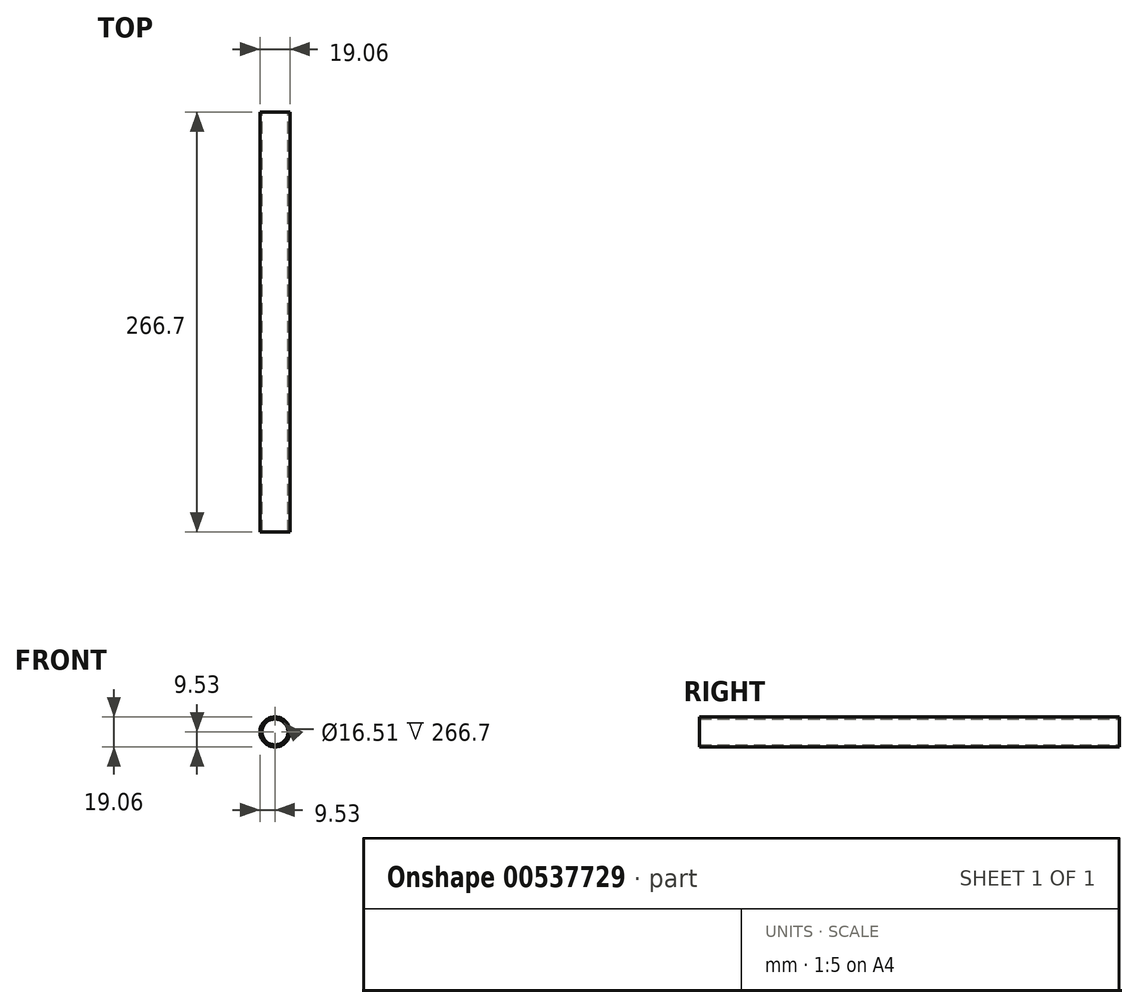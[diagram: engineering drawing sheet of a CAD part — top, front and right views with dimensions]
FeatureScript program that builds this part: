
annotation { "Feature Type Name" : "Feature", "Feature Type Description" : "" }
export const myFeature = defineFeature(function(context is Context, id is Id, definition is map)
    precondition{}
    {
        {
            var Q0;
            Q0=qCreatedBy(makeId("Front.planeOp"),FACE);
            var sketch = newSketch(context, id + "F0", { "sketchPlane" : qUnion([Q0])});
            skCircle(sketch, "E0", {"center": v(0, 0) * mm, "radius": 9.53 * mm});
            skSolve(sketch);
        }
        {
            var Q0;
            Q0 = qSketchRegion(id + "F0", true);
            extrude(context, id + "F1", {"entities" : qUnion([Q0]), "depth" : 266.7 * mm, "offsetDistance" : 25.4 * mm});
        }
        {
            var Q0;
            Q0=qCreatedBy(makeId("Front.planeOp"),FACE);
            var sketch = newSketch(context, id + "F2", { "sketchPlane" : qUnion([Q0])});
            skCircle(sketch, "E1", {"center": v(0, 0) * mm, "radius": 8.26 * mm});
            skSolve(sketch);
        }
        {
            var Q0;
            Q0 = qSketchRegion(id + "F2", true);
            extrude(context, id + "F3", {"entities" : qUnion([Q0]), "operationType" : NewBodyOperationType.REMOVE, "depth" : 266.7 * mm, "offsetDistance" : 25.4 * mm});
        }
    });
